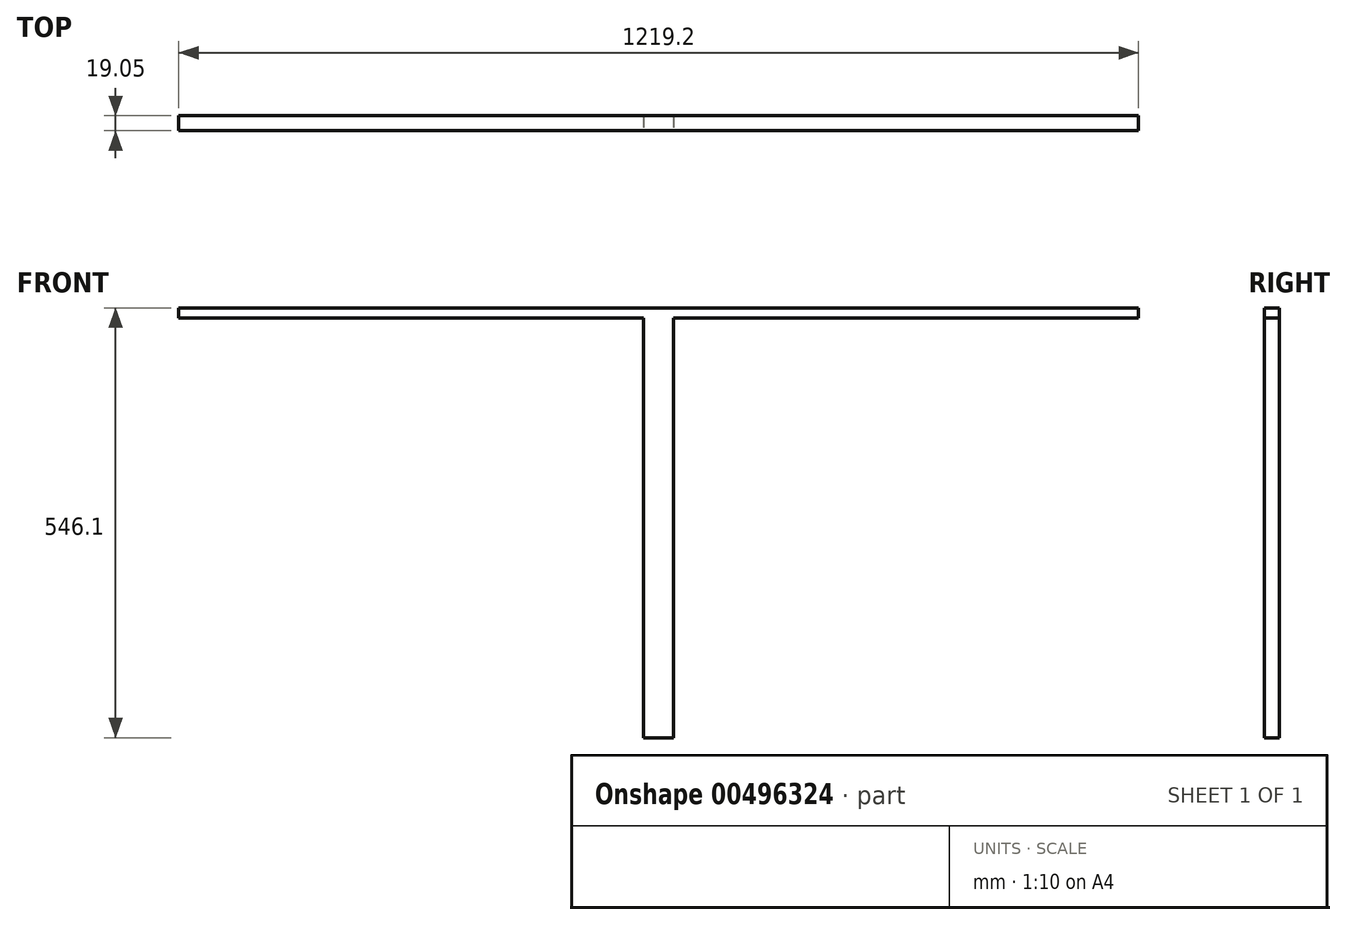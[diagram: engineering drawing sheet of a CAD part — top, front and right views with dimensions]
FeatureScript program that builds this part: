
annotation { "Feature Type Name" : "Feature", "Feature Type Description" : "" }
export const myFeature = defineFeature(function(context is Context, id is Id, definition is map)
    precondition{}
    {
        {
            var Q0;
            Q0=qCreatedBy(makeId("Front.planeOp"),FACE);
            var sketch = newSketch(context, id + "F0", { "sketchPlane" : qUnion([Q0])});
            skLineSegment(sketch, "E0.bottom", {"start": v(609.6, -273.05) * mm, "end": v(-609.6, -273.05) * mm});
            skLineSegment(sketch, "E0.top", {"start": v(609.6, 273.05) * mm, "end": v(-609.6, 273.05) * mm});
            skLineSegment(sketch, "E0.left", {"start": v(609.6, -273.05) * mm, "end": v(609.6, 273.05) * mm});
            skLineSegment(sketch, "E0.right", {"start": v(-609.6, -273.05) * mm, "end": v(-609.6, 273.05) * mm});
            skPoint(sketch, "E0.middle", {"position": v(0, 0) * mm});
            skSolve(sketch);
        }
        {
            var Q0;
            Q0=qSketchRegion(id+"F0",true);
            extrude(context, id + "F1", {"entities" : qUnion([Q0]), "depth" : 19.05 * mm, "offsetDistance" : 25.4 * mm});
        }
        {
            var Q0;
            Q0=makeQuery(id+"F1.opExtrude","CAP_FACE",FACE,{"disambiguationData":[OSD([sQuery(id+"F0.wireOp",EDGE,"E0.bottom"),sQuery(id+"F0.wireOp",EDGE,"E0.top"),sQuery(id+"F0.wireOp",EDGE,"E0.left"),sQuery(id+"F0.wireOp",EDGE,"E0.right")])],"isStart":false});
            var sketch = newSketch(context, id + "F2", { "sketchPlane" : qUnion([Q0])});
            skLineSegment(sketch, "E1.bottom", {"start": v(-609.6, -273.05) * mm, "end": v(-19.05, -273.05) * mm});
            skLineSegment(sketch, "E1.top", {"start": v(-609.6, 260.35) * mm, "end": v(-19.05, 260.35) * mm});
            skLineSegment(sketch, "E1.left", {"start": v(-609.6, -273.05) * mm, "end": v(-609.6, 260.35) * mm});
            skLineSegment(sketch, "E1.right", {"start": v(-19.05, -273.05) * mm, "end": v(-19.05, 260.35) * mm});
            skLineSegment(sketch, "E2.MirrorCS", {"start": v(19.05, -273.05) * mm, "end": v(19.05, 260.35) * mm});
            skLineSegment(sketch, "E3.MirrorCS", {"start": v(609.6, 260.35) * mm, "end": v(19.05, 260.35) * mm});
            skLineSegment(sketch, "E4.MirrorCS", {"start": v(609.6, -273.05) * mm, "end": v(609.6, 260.35) * mm});
            skLineSegment(sketch, "E5.MirrorCS", {"start": v(609.6, -273.05) * mm, "end": v(19.05, -273.05) * mm});
            skSolve(sketch);
        }
        {
            var Q0;
            Q0 = qSketchRegion(id + "F2", true);
            extrude(context, id + "F3", {"entities" : qUnion([Q0]), "operationType" : NewBodyOperationType.REMOVE, "oppositeDirection" : true, "depth" : 25.4 * mm});
        }
    });
